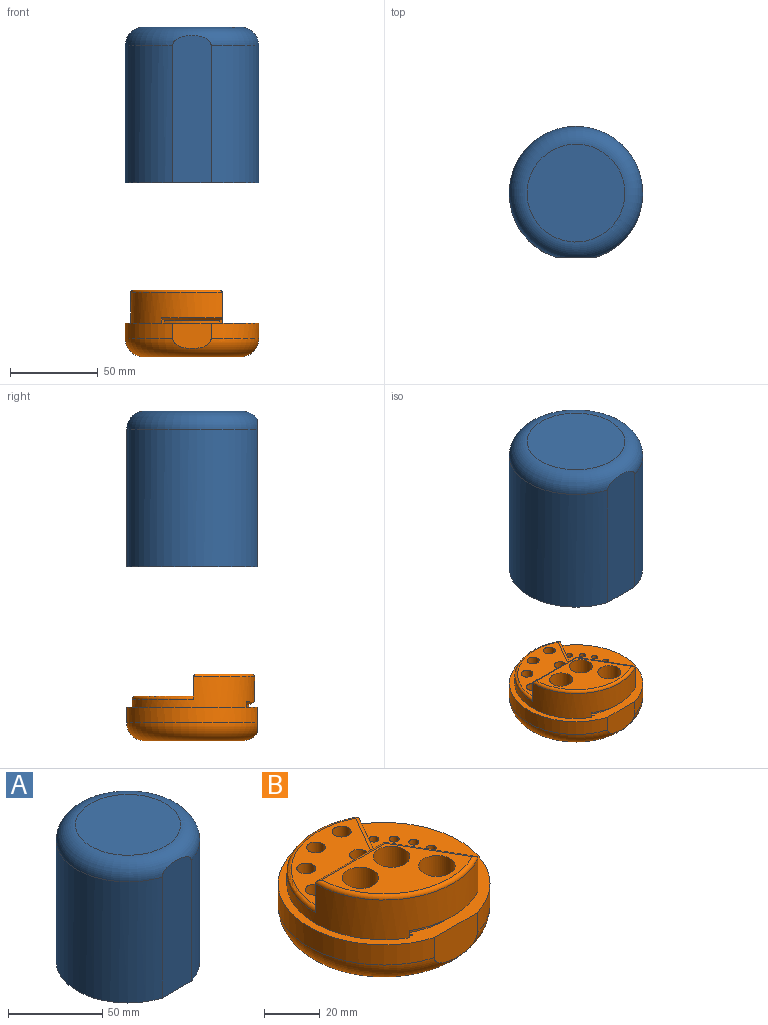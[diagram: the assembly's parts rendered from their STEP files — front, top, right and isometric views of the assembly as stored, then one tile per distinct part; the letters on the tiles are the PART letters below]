
ASSEMBLY  parts=2 mates=1
PART A: 14 faces, bbox 79.7x79.7x88.9 mm
  f0: cylinder r=38.1mm len=78.74mm, axis (0,0,-1), area 17111.4mm2, adj f1,f2,f11
  f1: plane 76.2x74.61mm, normal (0,0,-1), area 815.4mm2, adj f0,f4,f7,f9,f10,f11,f13
  f2: torus R=27.94mm, axis (0,0,1), area 3351.4mm2, adj f0,f3,f11
  f3: plane 55.88x55.88mm, normal (0,0,1), area 2452.5mm2, adj f2
  f4: cylinder r=34.92mm len=75.57mm, axis (0,0,-1), area 16465.9mm2, adj f1,f6,f8,f9,f10
  f5: plane 49.53x49.53mm, normal (0,0,-1), area 1926.8mm2, adj f6
  f6: torus R=24.77mm, axis (0,0,-1), area 3131.9mm2, adj f4,f5
  f7: cylinder r=31.75mm len=31.75mm, axis (0,0,-1), area 52.8mm2, adj f1,f8,f9,f10
  f8: cone r=31.75mm half-angle=63.4deg, axis (0,0,1), area 123.9mm2, adj f4,f7,f9,f10
  f9: plane 3.18x2.75mm, normal (0.87,0.5,0), area 7.6mm2, adj f1,f4,f7,f8
  f10: plane 3.18x2.75mm, normal (-0.87,0.5,0), area 7.6mm2, adj f1,f4,f7,f8
  f11: plane 84.19x21.77mm, normal (0,-1,0), area 1807.9mm2, adj f0,f1,f2
  f12: plane 0.31x0.31mm, normal (0,0,-1), area 0.1mm2, adj f13
  f13: torus R=0.16mm, axis (0,0,-1), area 0.6mm2, adj f1,f12
PART B: 65 faces, bbox 82.5x82.5x38.1 mm
  f0: cylinder r=38.1mm len=76.2mm, axis (0,0,-1), area 1931.9mm2, adj f1,f2,f57
  f1: plane 76.2x74.61mm, normal (0,0,1), area 1962.5mm2, adj f0,f6,f7,f27,f29,f31,f33,f35
  f2: torus R=27.94mm, axis (0,0,1), area 3351.5mm2, adj f0,f8,f57
  f3: plane 48.57x31.75mm, normal (0,0,1), area 655.3mm2, adj f9,f11,f13,f62,f63,f64
  f4: plane 34.93x12.7mm, normal (0,1,0), area 389.3mm2, adj f5,f7,f53,f60,f61,f62
  f5: plane 48.61x33.34mm, normal (0,0,1), area 895.7mm2, adj f4,f15,f17,f19,f21,f23,f25,f60
  f6: plane 30.25x17.46mm, normal (0.87,-0.5,0), area 166.3mm2, adj f1,f7,f53,f60
  f7: plane 30.25x17.46mm, normal (0.87,0.5,0), area 602.3mm2, adj f1,f4,f6,f53,f54,f55,f63
  f8: plane 55.88x55.88mm, normal (0,0,-1), area 2452.5mm2, adj f2
  f9: cylinder r=6.55mm len=31.75mm, axis (0,0,1), area 1306.4mm2, adj f3,f10
  f10: plane 13.1x13.1mm, normal (0,0,1), area 134.7mm2, adj f9
  f11: cylinder r=6.55mm len=31.75mm, axis (0,0,1), area 1306.4mm2, adj f3,f12
  f12: plane 13.1x13.1mm, normal (0,0,1), area 134.7mm2, adj f11
  f13: cylinder r=6.55mm len=31.75mm, axis (0,0,1), area 1306.4mm2, adj f3,f14
  f14: plane 13.1x13.1mm, normal (0,0,1), area 134.7mm2, adj f13
  f15: cylinder r=3.37mm len=12.7mm, axis (0,0,1), area 269.2mm2, adj f5,f16
  f16: plane 6.75x6.75mm, normal (0,0,1), area 35.8mm2, adj f15
  f17: cylinder r=3.37mm len=12.7mm, axis (0,0,1), area 269.2mm2, adj f5,f18
  f18: plane 6.75x6.75mm, normal (0,0,1), area 35.8mm2, adj f17
  f19: cylinder r=3.37mm len=12.7mm, axis (0,0,1), area 269.2mm2, adj f5,f20
  f20: plane 6.75x6.75mm, normal (0,0,1), area 35.8mm2, adj f19
  f21: cylinder r=3.37mm len=12.7mm, axis (0,0,1), area 269.2mm2, adj f5,f22
  f22: plane 6.75x6.75mm, normal (0,0,1), area 35.8mm2, adj f21
  f23: cylinder r=3.37mm len=12.7mm, axis (0,0,1), area 269.2mm2, adj f5,f24
  f24: plane 6.75x6.75mm, normal (0,0,1), area 35.8mm2, adj f23
  f25: cylinder r=3.37mm len=12.7mm, axis (0,0,1), area 269.2mm2, adj f5,f26
  f26: plane 6.75x6.75mm, normal (0,0,1), area 35.8mm2, adj f25
  f27: cylinder r=1.79mm len=7.62mm, axis (0,0,1), area 85.5mm2, adj f1,f28
  f28: plane 3.57x3.57mm, normal (0,0,1), area 10mm2, adj f27
  f29: cylinder r=1.79mm len=7.62mm, axis (0,0,1), area 85.5mm2, adj f1,f30
  f30: plane 3.57x3.57mm, normal (0,0,1), area 10mm2, adj f29
  f31: cylinder r=1.79mm len=7.62mm, axis (0,0,1), area 85.5mm2, adj f1,f32
  f32: plane 3.57x3.57mm, normal (0,0,1), area 10mm2, adj f31
  f33: cylinder r=1.79mm len=7.62mm, axis (0,0,1), area 85.5mm2, adj f1,f34
  f34: plane 3.57x3.57mm, normal (0,0,1), area 10mm2, adj f33
  f35: cylinder r=1.79mm len=7.62mm, axis (0,0,1), area 85.5mm2, adj f1,f36
  f36: plane 3.57x3.57mm, normal (0,0,1), area 10mm2, adj f35
  f37: cylinder r=1.79mm len=7.62mm, axis (0,0,1), area 85.5mm2, adj f1,f38
  f38: plane 3.57x3.57mm, normal (0,0,1), area 10mm2, adj f37
  f39: cylinder r=1.79mm len=7.62mm, axis (0,0,1), area 85.5mm2, adj f1,f40
  f40: plane 3.57x3.57mm, normal (0,0,1), area 10mm2, adj f39
  f41: cylinder r=1.79mm len=7.62mm, axis (0,0,1), area 85.5mm2, adj f1,f42
  f42: plane 3.57x3.57mm, normal (0,0,1), area 10mm2, adj f41
  f43: cylinder r=1.79mm len=7.62mm, axis (0,0,1), area 85.5mm2, adj f1,f44
  f44: plane 3.57x3.57mm, normal (0,0,1), area 10mm2, adj f43
  f45: cylinder r=1.79mm len=7.62mm, axis (0,0,1), area 85.5mm2, adj f1,f46
  f46: plane 3.57x3.57mm, normal (0,0,1), area 10mm2, adj f45
  f47: cylinder r=1.79mm len=7.62mm, axis (0,0,1), area 85.5mm2, adj f1,f48
  f48: plane 3.57x3.57mm, normal (0,0,1), area 10mm2, adj f47
  f49: cylinder r=1.79mm len=7.62mm, axis (0,0,1), area 85.5mm2, adj f1,f50
  f50: plane 3.57x3.57mm, normal (0,0,1), area 10mm2, adj f49
  f51: cylinder r=1.79mm len=7.62mm, axis (0,0,1), area 85.5mm2, adj f1,f52
  f52: plane 3.57x3.57mm, normal (0,0,1), area 10mm2, adj f51
  f53: cylinder r=34.92mm len=69.85mm, axis (0,0,-1), area 1509.6mm2, adj f1,f4,f6,f7,f55,f56,f61,f64
  f54: cylinder r=31.75mm len=31.75mm, axis (0,0,-1), area 52.8mm2, adj f1,f7,f55,f56
  f55: cone r=31.75mm half-angle=63.4deg, axis (0,0,1), area 123.9mm2, adj f7,f53,f54,f56
  f56: plane 3.18x2.75mm, normal (0.87,-0.5,0), area 7.6mm2, adj f1,f53,f54,f55
  f57: plane 21.77x14.34mm, normal (0,-1,0), area 287.5mm2, adj f0,f1,f2
  f58: plane 0.31x0.31mm, normal (0,0,1), area 0.1mm2, adj f59
  f59: torus R=0.16mm, axis (0,0,-1), area 0.6mm2, adj f1,f58
  f60: cylinder r=1.59mm len=31.83mm, axis (0.5,0.87,0), area 86.5mm2, adj f4,f5,f6,f61
  f61: torus R=33.34mm, axis (0,0,1), area 178mm2, adj f4,f5,f53,f60
  f62: cylinder r=1.59mm len=34.93mm, axis (-1,0,0), area 84.8mm2, adj f3,f4,f63,f64
  f63: cylinder r=1.59mm len=31.04mm, axis (-0.5,0.87,0), area 84.8mm2, adj f3,f7,f62,f64
  f64: torus R=33.34mm, axis (0,0,1), area 176.5mm2, adj f3,f53,f62,f63
PLACE A t=(0,0,80.17)mm
PLACE B at identity
MATE slider B.f0 <-> A.f6  axis (0,0,1) through (0,0,19.05)mm
